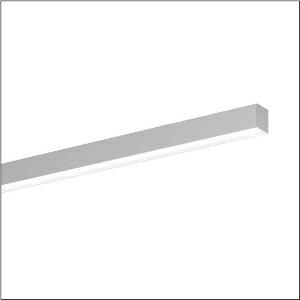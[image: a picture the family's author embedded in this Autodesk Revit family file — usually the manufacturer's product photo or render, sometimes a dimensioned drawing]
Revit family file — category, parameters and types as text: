
# Revit family: silica_r__21_51mx23da34sb_798d
name_source: partatom
category: Lighting Fixtures
units: mm (PartAtom-declared; Revit-internal decimal feet)

## family parameters
Cut with Voids When Loaded = No
Host = Face
Light Source = No
Part Type = Normal
Room Calculation Point = No
Round Connector Dimension = Use Diameter
Shared = No

## types (1)
- --- (1 x LED, 3280 lm, 24.1 W, 3000K)
    Apparent Load = 24 VA
    CIE Flux Codes = 78 96 99 100 100
    Color Rendering = 80
    Color Temperature = 3000K
    Default Elevation = 1800 mm
    Description = Silica® 21, office luminaire, primary optical cover: prismatic diffuser, of PMMA, CAT 2 (L<= 3000cd/m²), light emission: direct distribution, primary light characteristic: symmetric, installation type: surface-mounted, LED, rated luminous flux: 3.280lm, luminous efficacy: 136lm/W, light colour: 830, colour temperature: 3000K, with terminal, 3+2-pole, max. 2.5mm², mains connection: 220..240V, AC, 50/60Hz, rated input power: 24.1W, luminaire housing, of aluminium, metallic grey (RAL 9006), length: 1.204mm, width: 53mm, height: 53mm, protection rating (complete): IP20, insulation class (complete): insulation class I (protective earthing), certification: CE, permissible operating ambient temperature: 0..+35°C, standard: EN 50419, packaging unit: 1 piece
    Height = 0 mm  [stored 0 ft]
    Lamp = 1 x LED
    Lamp Light Flux = 3280 lm
    Lamp Power = 24.1 W
    Lamp count = 1
    Length = 1204 mm
    Luminous efficacy = 136 lm/W
    Manufacturer = Siteco
    ModVariant = No
    Model = 51MX23DA34SB
    Mounting Place = Ceiling
    Mounting Type = Recessed
    Number of Poles = 1
    OnlyDefault = Yes
    Power Factor = 1
    Product Name = Silica® 21
    Product group = office luminaire | ceiling recessed
    ProductGroupID = 401
    Protection Class = Protection class I
    Protection Degree = IP 20
    RLX_Detail_Level = 1
    RLX_Emergency_Light_Flux = 0 lm
    RLX_Emergency_Type = 0
    RLX_Emergency_Type_DB = No
    RlxData = <blob elided: 21401 chars, md5=df1accfb>
    Socket = socket
    Standby Power = 0 W
    System Light Flux = 3280 lm
    System Power = 24 W
    Type Comments = factory setting: luminous flux: 100 % | dim-lin: 254 | 345 mA
    Type Image = l_1297768.jpg
    URL = http://relux.com
    VarID = @adj_049739
    Voltage = 0 V
    Weight = 0.00 kg
    Width = 53 mm

note: [stored X ft] marks values corroborated as IEEE doubles in the binary element streams (Revit-internal decimal feet)

## geometry (parser evidence)
native form markers: Blend x4, Sweep x9
no freeform markers — native parametric forms only
